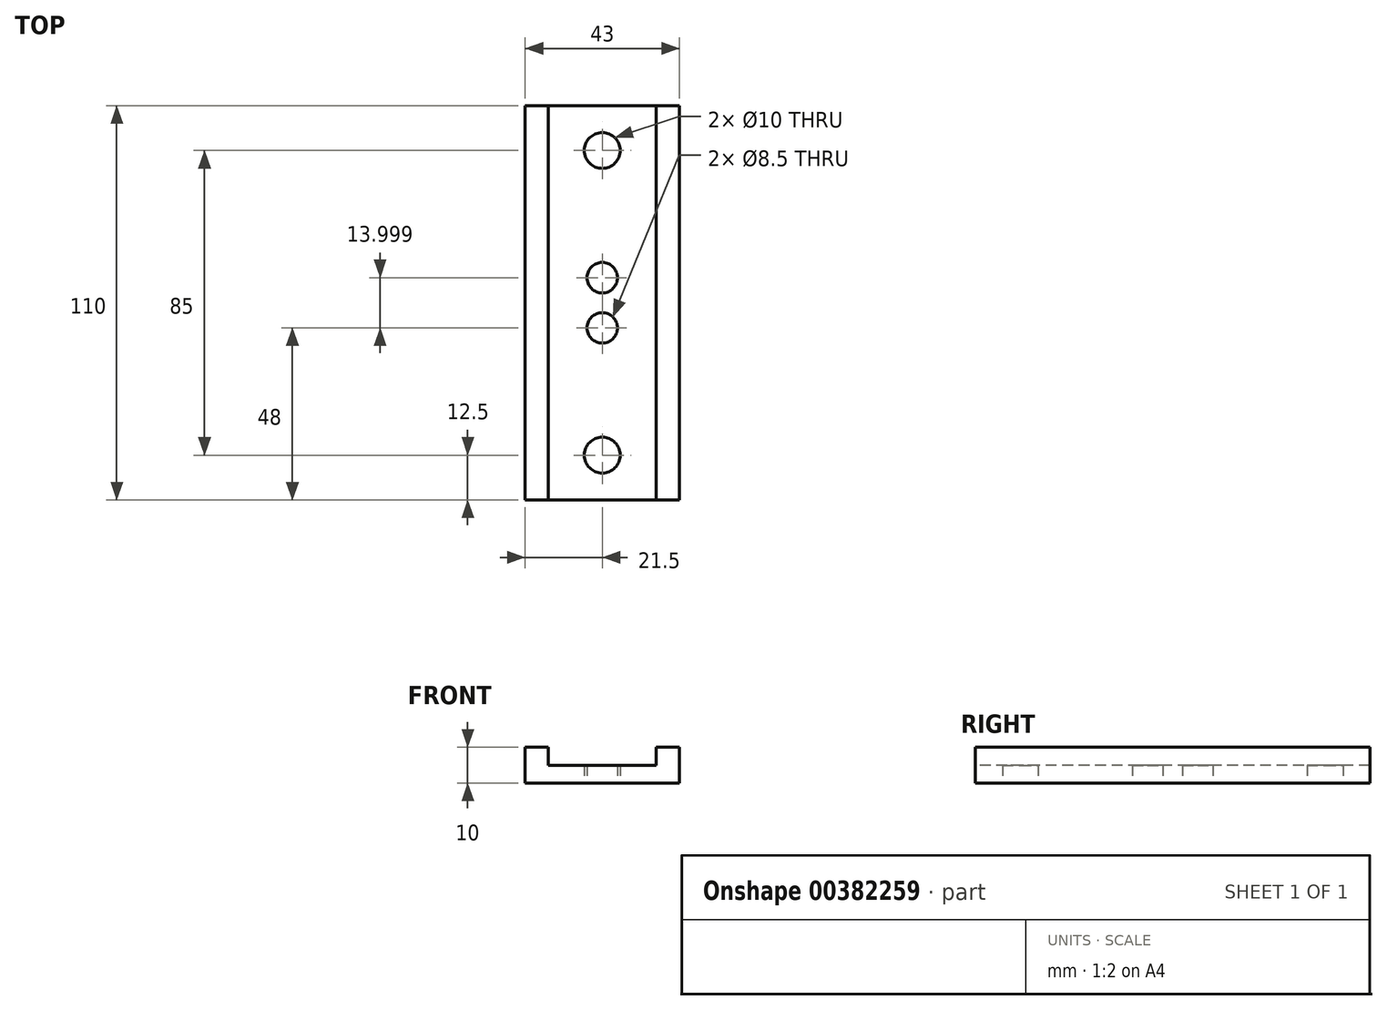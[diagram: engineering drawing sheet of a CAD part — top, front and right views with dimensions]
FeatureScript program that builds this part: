
annotation { "Feature Type Name" : "Feature", "Feature Type Description" : "" }
export const myFeature = defineFeature(function(context is Context, id is Id, definition is map)
    precondition{}
    {
        {
            var Q0;
            Q0=qCreatedBy(makeId("Top.planeOp"),FACE);
            var sketch = newSketch(context, id + "F0", { "sketchPlane" : qUnion([Q0])});
            skLineSegment(sketch, "E0.bottom", {"start": v(21.5, 55) * mm, "end": v(-21.5, 55) * mm});
            skLineSegment(sketch, "E0.top", {"start": v(21.5, -55) * mm, "end": v(-21.5, -55) * mm});
            skLineSegment(sketch, "E0.left", {"start": v(21.5, 55) * mm, "end": v(21.5, -55) * mm});
            skLineSegment(sketch, "E0.right", {"start": v(-21.5, 55) * mm, "end": v(-21.5, -55) * mm});
            skPoint(sketch, "E0.middle", {"position": v(0, 0) * mm});
            skCircle(sketch, "E1", {"center": v(0, 7) * mm, "radius": 4.25 * mm});
            skCircle(sketch, "E2.MirrorC", {"center": v(0, -7) * mm, "radius": 4.25 * mm});
            skCircle(sketch, "E3", {"center": v(0, 42.5) * mm, "radius": 5 * mm});
            skCircle(sketch, "E4", {"center": v(0, -42.5) * mm, "radius": 5 * mm});
            skSolve(sketch);
        }
        {
            var Q0;
            Q0=makeQuery(id+"F0.imprint","IMPRINT",FACE,{"disambiguationData":[TD([[makeQuery(id+"F0.imprint","IMPRINT",EDGE,{"derivedFrom":sQuery(id+"F0.wireOp",EDGE,"E0.bottom")}),1.0]])]});
            extrude(context, id + "F1", {"entities" : qUnion([Q0]), "depth" : 5 * mm});
        }
        {
            var Q0;
            Q0=makeQuery(id+"F1.opExtrude","CAP_FACE",FACE,{"disambiguationData":[OSD([sQuery(id+"F0.wireOp",EDGE,"E0.bottom"),sQuery(id+"F0.wireOp",EDGE,"E0.top"),sQuery(id+"F0.wireOp",EDGE,"E0.left"),sQuery(id+"F0.wireOp",EDGE,"E0.right"),sQuery(id+"F0.wireOp",EDGE,"E1"),sQuery(id+"F0.wireOp",EDGE,"E2.MirrorC"),sQuery(id+"F0.wireOp",EDGE,"E3"),sQuery(id+"F0.wireOp",EDGE,"E4")])],"isStart":false});
            var sketch = newSketch(context, id + "F2", { "sketchPlane" : qUnion([Q0])});
            skLineSegment(sketch, "E5.bottom", {"start": v(-21.5, 55) * mm, "end": v(-15, 55) * mm});
            skLineSegment(sketch, "E5.top", {"start": v(-21.5, -55) * mm, "end": v(-15, -55) * mm});
            skLineSegment(sketch, "E5.left", {"start": v(-21.5, 55) * mm, "end": v(-21.5, -55) * mm});
            skLineSegment(sketch, "E5.right", {"start": v(-15, 55) * mm, "end": v(-15, -55) * mm});
            skLineSegment(sketch, "E6.bottom", {"start": v(21.5, 55) * mm, "end": v(15, 55) * mm});
            skLineSegment(sketch, "E6.top", {"start": v(21.5, -55) * mm, "end": v(15, -55) * mm});
            skLineSegment(sketch, "E6.left", {"start": v(21.5, 55) * mm, "end": v(21.5, -55) * mm});
            skLineSegment(sketch, "E6.right", {"start": v(15, 55) * mm, "end": v(15, -55) * mm});
            skSolve(sketch);
        }
        {
            var Q0;
            Q0=makeQuery(id+"F2.imprint","IMPRINT",FACE,{"disambiguationData":[TD([[makeQuery(id+"F2.imprint","IMPRINT",EDGE,{"derivedFrom":sQuery(id+"F2.wireOp",EDGE,"E5.bottom")}),1.0]])]});
            var Q1;
            Q1=makeQuery(id+"F2.imprint","IMPRINT",FACE,{"disambiguationData":[TD([[makeQuery(id+"F2.imprint","IMPRINT",EDGE,{"derivedFrom":sQuery(id+"F2.wireOp",EDGE,"E6.bottom")}),1.0]])]});
            extrude(context, id + "F3", {"entities" : qUnion([Q0, Q1]), "operationType" : NewBodyOperationType.ADD, "depth" : 5 * mm});
        }
    });
